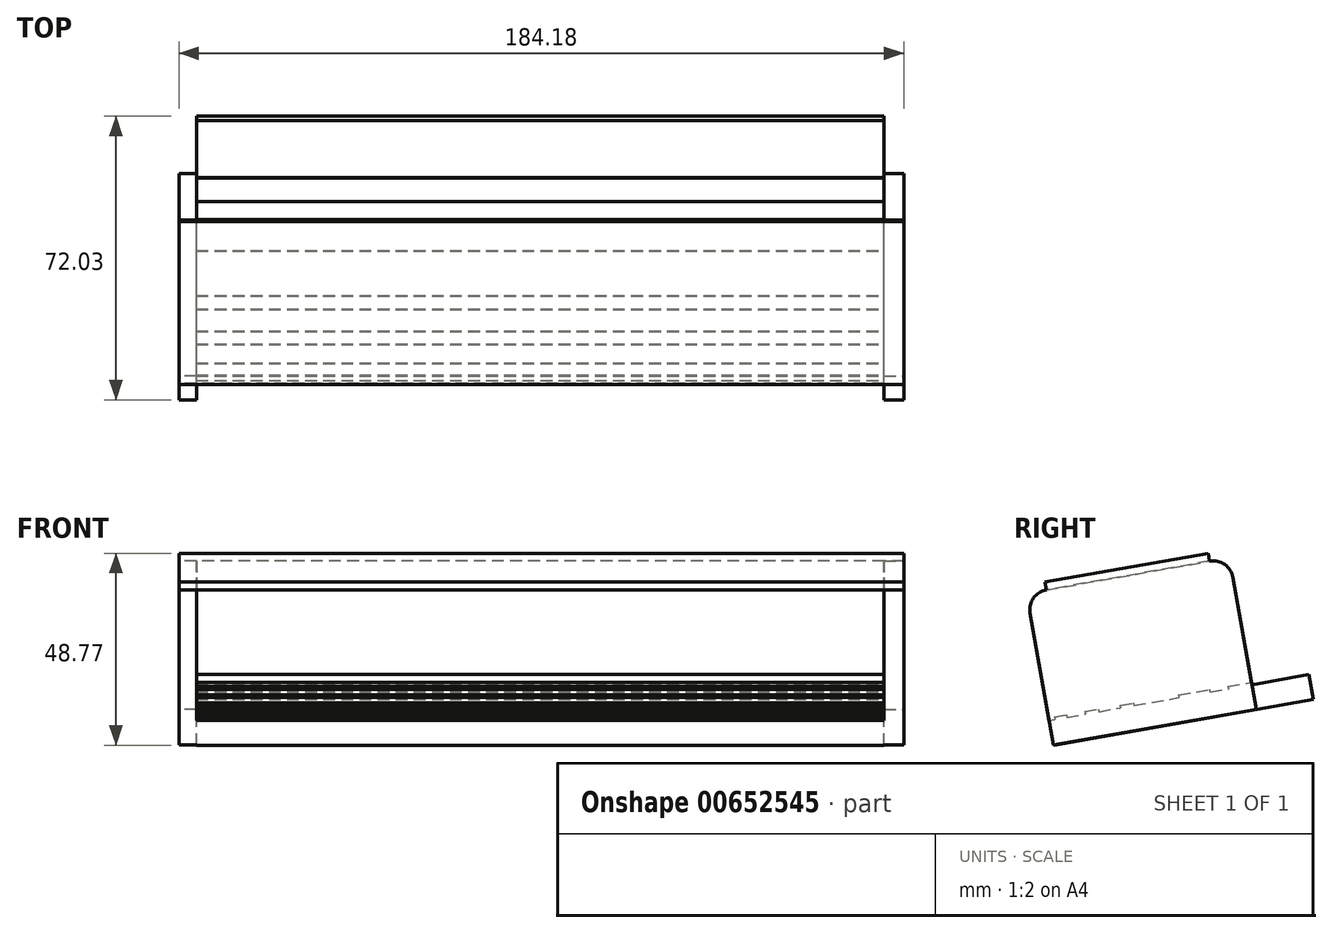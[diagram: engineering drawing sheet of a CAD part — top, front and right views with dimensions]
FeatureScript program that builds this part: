
annotation { "Feature Type Name" : "Feature", "Feature Type Description" : "" }
export const myFeature = defineFeature(function(context is Context, id is Id, definition is map)
    precondition{}
    {
        {
            var Q0;
            Q0=qCreatedBy(makeId("Front.planeOp"),FACE);
            var sketch = newSketch(context, id + "F0", { "sketchPlane" : qUnion([Q0])});
            skLineSegment(sketch, "E0.bottom", {"start": v(-82.9, 3.26) * mm, "end": v(91.78, 3.26) * mm});
            skLineSegment(sketch, "E0.top", {"start": v(-82.9, -3.13) * mm, "end": v(91.78, -3.13) * mm});
            skLineSegment(sketch, "E0.left", {"start": v(-82.9, 3.26) * mm, "end": v(-82.9, -3.13) * mm});
            skLineSegment(sketch, "E0.right", {"start": v(91.78, 3.26) * mm, "end": v(91.78, -3.13) * mm});
            skSolve(sketch);
        }
        {
            var Q0;
            Q0=qSketchRegion(id+"F0",true);
            var Q1;
            Q1=sQuery(id+"F0.wireOp",EDGE,"E0.top");
            var Q2;
            Q2=sQuery(id+"F0.wireOp",EDGE,"E0.left");
            var Q3;
            Q3=sQuery(id+"F0.wireOp",EDGE,"E0.right");
            extrude(context, id + "F1", {"entities" : qUnion([Q0]), "surfaceEntities" : qUnion([Q1, Q2, Q3]), "depth" : 67.06 * mm, "offsetDistance" : 25.4 * mm});
        }
        {
            var Q0;
            Q0=makeQuery(id+"F1.opExtrude","SWEPT_BODY",BODY,{"disambiguationData":[OSD([sQuery(id+"F0.wireOp",EDGE,"E0.bottom"),sQuery(id+"F0.wireOp",EDGE,"E0.top"),sQuery(id+"F0.wireOp",EDGE,"E0.left"),sQuery(id+"F0.wireOp",EDGE,"E0.right")])]});
            var Q1;
            Q1=makeQuery(id+"F1.opExtrude","CAP_EDGE",EDGE,{"disambiguationData":[OSD([sQuery(id+"F0.wireOp",EDGE,"E0.bottom")])],"isStart":true});
            transform(context, id + "F2", {"entities" : qUnion([Q0]), "transformType" : TransformType.ROTATION, "transformAxis" : qUnion([Q1]), "angle" : 10 * degree, "makeCopy" : false});
        }
        {
            var Q0;
            Q0=makeQuery(id+"F1.opExtrude","SWEPT_FACE",FACE,{"disambiguationData":[OSD([sQuery(id+"F0.wireOp",EDGE,"E0.bottom")])]});
            var sketch = newSketch(context, id + "F3", { "sketchPlane" : qUnion([Q0])});
            skLineSegment(sketch, "E1.bottom", {"start": v(-82.9, -65.03) * mm, "end": v(91.78, -65.03) * mm});
            skLineSegment(sketch, "E1.top", {"start": v(-82.9, -61.92) * mm, "end": v(91.78, -61.92) * mm});
            skLineSegment(sketch, "E1.left", {"start": v(-82.9, -65.03) * mm, "end": v(-82.9, -61.92) * mm});
            skLineSegment(sketch, "E1.right", {"start": v(91.78, -65.03) * mm, "end": v(91.78, -61.92) * mm});
            skLineSegment(sketch, "E2.bottom", {"start": v(-82.9, -57.1) * mm, "end": v(91.78, -57.1) * mm});
            skLineSegment(sketch, "E2.top", {"start": v(-82.9, -53.67) * mm, "end": v(91.78, -53.67) * mm});
            skLineSegment(sketch, "E2.left", {"start": v(-82.9, -57.1) * mm, "end": v(-82.9, -53.67) * mm});
            skLineSegment(sketch, "E2.right", {"start": v(91.78, -57.1) * mm, "end": v(91.78, -53.67) * mm});
            skLineSegment(sketch, "E3.bottom", {"start": v(-82.9, -48.06) * mm, "end": v(91.78, -48.06) * mm});
            skLineSegment(sketch, "E3.top", {"start": v(-82.9, -44.61) * mm, "end": v(91.78, -44.61) * mm});
            skLineSegment(sketch, "E3.left", {"start": v(-82.9, -48.06) * mm, "end": v(-82.9, -44.61) * mm});
            skLineSegment(sketch, "E3.right", {"start": v(91.78, -48.06) * mm, "end": v(91.78, -44.61) * mm});
            skLineSegment(sketch, "E4.bottom", {"start": v(-82.9, -32.96) * mm, "end": v(91.78, -32.96) * mm});
            skLineSegment(sketch, "E4.top", {"start": v(-82.9, -36.02) * mm, "end": v(91.78, -36.02) * mm});
            skLineSegment(sketch, "E4.left", {"start": v(-82.9, -36.02) * mm, "end": v(-82.9, -32.96) * mm});
            skLineSegment(sketch, "E4.right", {"start": v(91.78, -36.02) * mm, "end": v(91.78, -32.96) * mm});
            skLineSegment(sketch, "E5.bottom", {"start": v(-82.9, -29.61) * mm, "end": v(91.78, -29.61) * mm});
            skLineSegment(sketch, "E5.top", {"start": v(-82.9, -24.95) * mm, "end": v(91.78, -24.95) * mm});
            skLineSegment(sketch, "E5.left", {"start": v(-82.9, -29.61) * mm, "end": v(-82.9, -24.95) * mm});
            skLineSegment(sketch, "E5.right", {"start": v(91.78, -29.61) * mm, "end": v(91.78, -24.95) * mm});
            skLineSegment(sketch, "E6.bottom", {"start": v(-82.9, -20.2) * mm, "end": v(91.78, -20.2) * mm});
            skLineSegment(sketch, "E6.top", {"start": v(-82.9, -14.17) * mm, "end": v(91.78, -14.17) * mm});
            skLineSegment(sketch, "E6.left", {"start": v(-82.9, -20.2) * mm, "end": v(-82.9, -14.17) * mm});
            skLineSegment(sketch, "E6.right", {"start": v(91.78, -20.2) * mm, "end": v(91.78, -14.17) * mm});
            skPoint(sketch, "E7.oppositeSnap0", {"position": v(-79.18, -5.35) * mm});
            skLineSegment(sketch, "E8.left", {"start": v(91.78, -66.49) * mm, "end": v(91.78, -9.05) * mm});
            skLineSegment(sketch, "E9.bottom", {"start": v(-82.9, -14.17) * mm, "end": v(-87.37, -14.17) * mm});
            skLineSegment(sketch, "E9.top", {"start": v(-82.9, -66.49) * mm, "end": v(-87.37, -66.49) * mm});
            skLineSegment(sketch, "E9.left", {"start": v(-82.9, -14.17) * mm, "end": v(-82.9, -66.49) * mm});
            skLineSegment(sketch, "E9.right", {"start": v(-87.37, -14.17) * mm, "end": v(-87.37, -66.49) * mm});
            skLineSegment(sketch, "E10.bottom", {"start": v(91.78, -66.49) * mm, "end": v(96.81, -66.49) * mm});
            skLineSegment(sketch, "E10.top", {"start": v(91.78, -14.17) * mm, "end": v(96.81, -14.17) * mm});
            skLineSegment(sketch, "E10.left", {"start": v(91.78, -66.49) * mm, "end": v(91.78, -14.17) * mm});
            skLineSegment(sketch, "E10.right", {"start": v(96.81, -66.49) * mm, "end": v(96.81, -14.17) * mm});
            skSolve(sketch);
        }
        {
            var Q0;
            Q0=makeQuery(id+"F3.imprint","IMPRINT",FACE,{"disambiguationData":[TD([[makeQuery(id+"F3.imprint","IMPRINT",EDGE,{"derivedFrom":sQuery(id+"F3.wireOp",EDGE,"E6.bottom")}),1.0]])]});
            var Q1;
            Q1=makeQuery(id+"F3.imprint","IMPRINT",FACE,{"disambiguationData":[TD([[makeQuery(id+"F3.imprint","IMPRINT",EDGE,{"derivedFrom":sQuery(id+"F3.wireOp",EDGE,"E4.bottom")}),1.0]])]});
            var Q2;
            Q2=makeQuery(id+"F3.imprint","IMPRINT",FACE,{"disambiguationData":[TD([[makeQuery(id+"F3.imprint","IMPRINT",EDGE,{"derivedFrom":sQuery(id+"F3.wireOp",EDGE,"E5.bottom")}),1.0]])]});
            var Q3;
            Q3=makeQuery(id+"F3.imprint","IMPRINT",FACE,{"disambiguationData":[TD([[makeQuery(id+"F3.imprint","IMPRINT",EDGE,{"derivedFrom":sQuery(id+"F3.wireOp",EDGE,"E3.bottom")}),1.0]])]});
            var Q4;
            Q4=makeQuery(id+"F3.imprint","IMPRINT",FACE,{"disambiguationData":[TD([[makeQuery(id+"F3.imprint","IMPRINT",EDGE,{"derivedFrom":sQuery(id+"F3.wireOp",EDGE,"E2.bottom")}),1.0]])]});
            var Q5;
            Q5=makeQuery(id+"F3.imprint","IMPRINT",FACE,{"disambiguationData":[TD([[makeQuery(id+"F3.imprint","IMPRINT",EDGE,{"derivedFrom":sQuery(id+"F3.wireOp",EDGE,"E1.bottom")}),1.0]])]});
            extrude(context, id + "F4", {"entities" : qUnion([Q0, Q1, Q2, Q3, Q4, Q5]), "operationType" : NewBodyOperationType.ADD, "depth" : 0.64 * mm, "offsetDistance" : 25.4 * mm});
        }
        {
            var Q0;
            {var subQ8=sQuery(id+"F3.wireOp",EDGE,"E9.bottom");Q0=makeQuery(id+"F3.imprint","IMPRINT",FACE,{"disambiguationData":[TD([[makeQuery(id+"F3.imprint","IMPRINT",EDGE,{"derivedFrom":subQ8}),1.0]])]});}
            var Q1;
            {var subQ8=sQuery(id+"F3.wireOp",EDGE,"E10.bottom");Q1=makeQuery(id+"F3.imprint","IMPRINT",FACE,{"disambiguationData":[TD([[makeQuery(id+"F3.imprint","IMPRINT",EDGE,{"derivedFrom":subQ8}),1.0]])]});}
            extrude(context, id + "F5", {"entities" : qUnion([Q0, Q1]), "operationType" : NewBodyOperationType.ADD, "depth" : 32.77 * mm, "offsetDistance" : 25.4 * mm, "hasSecondDirection" : true, "secondDirectionOppositeDirection" : true, "secondDirectionDepth" : 6.35 * mm});
        }
        {
            var Q0;
            Q0=makeQuery(id+"F5.opExtrude","CAP_EDGE",EDGE,{"disambiguationData":[OSD([sQuery(id+"F3.wireOp",EDGE,"E10.top")])],"isStart":false});
            var Q1;
            Q1=makeQuery(id+"F5.opExtrude","CAP_EDGE",EDGE,{"disambiguationData":[OSD([sQuery(id+"F3.wireOp",EDGE,"E9.bottom")])],"isStart":false});
            var Q2;
            Q2=makeQuery(id+"F5.opExtrude","CAP_EDGE",EDGE,{"disambiguationData":[OSD([sQuery(id+"F3.wireOp",EDGE,"E9.top")])],"isStart":false});
            var Q3;
            Q3=makeQuery(id+"F5.opExtrude","CAP_EDGE",EDGE,{"disambiguationData":[OSD([sQuery(id+"F3.wireOp",EDGE,"E10.bottom")])],"isStart":false});
            fillet(context, id + "F6", {"entities" : qUnion([Q0, Q1, Q2, Q3]), "radius" : 5.08 * mm, "tangentPropagation" : true, "allowEdgeOverflow" : false});
        }
        {
            var Q0;
            Q0=makeQuery(id+"F5.opExtrude","CAP_FACE",FACE,{"disambiguationData":[OSD([sQuery(id+"F3.wireOp",EDGE,"E10.bottom"),sQuery(id+"F3.wireOp",EDGE,"E10.top"),sQuery(id+"F3.wireOp",EDGE,"E10.left"),sQuery(id+"F3.wireOp",EDGE,"E10.right")])],"isStart":false});
            var sketch = newSketch(context, id + "F7", { "sketchPlane" : qUnion([Q0])});
            skLineSegment(sketch, "E11.bottom", {"start": v(96.81, -61.4) * mm, "end": v(-87.27, -61.4) * mm});
            skLineSegment(sketch, "E11.top", {"start": v(96.81, -19.29) * mm, "end": v(-87.27, -19.29) * mm});
            skLineSegment(sketch, "E11.left", {"start": v(96.81, -61.4) * mm, "end": v(96.81, -19.29) * mm});
            skLineSegment(sketch, "E11.right", {"start": v(-87.27, -61.4) * mm, "end": v(-87.27, -19.29) * mm});
            skSolve(sketch);
        }
        {
            var Q0;
            {var subQ4=sQuery(id+"F7.wireOp",EDGE,"E11.top");Q0=makeQuery(id+"F7.imprint","IMPRINT",FACE,{"disambiguationData":[TD([[makeQuery(id+"F7.imprint","IMPRINT",EDGE,{"derivedFrom":subQ4}),1.0]])]});}
            extrude(context, id + "F8", {"entities" : qUnion([Q0]), "operationType" : NewBodyOperationType.ADD, "depth" : 2.03 * mm, "offsetDistance" : 25.4 * mm});
        }
    });
